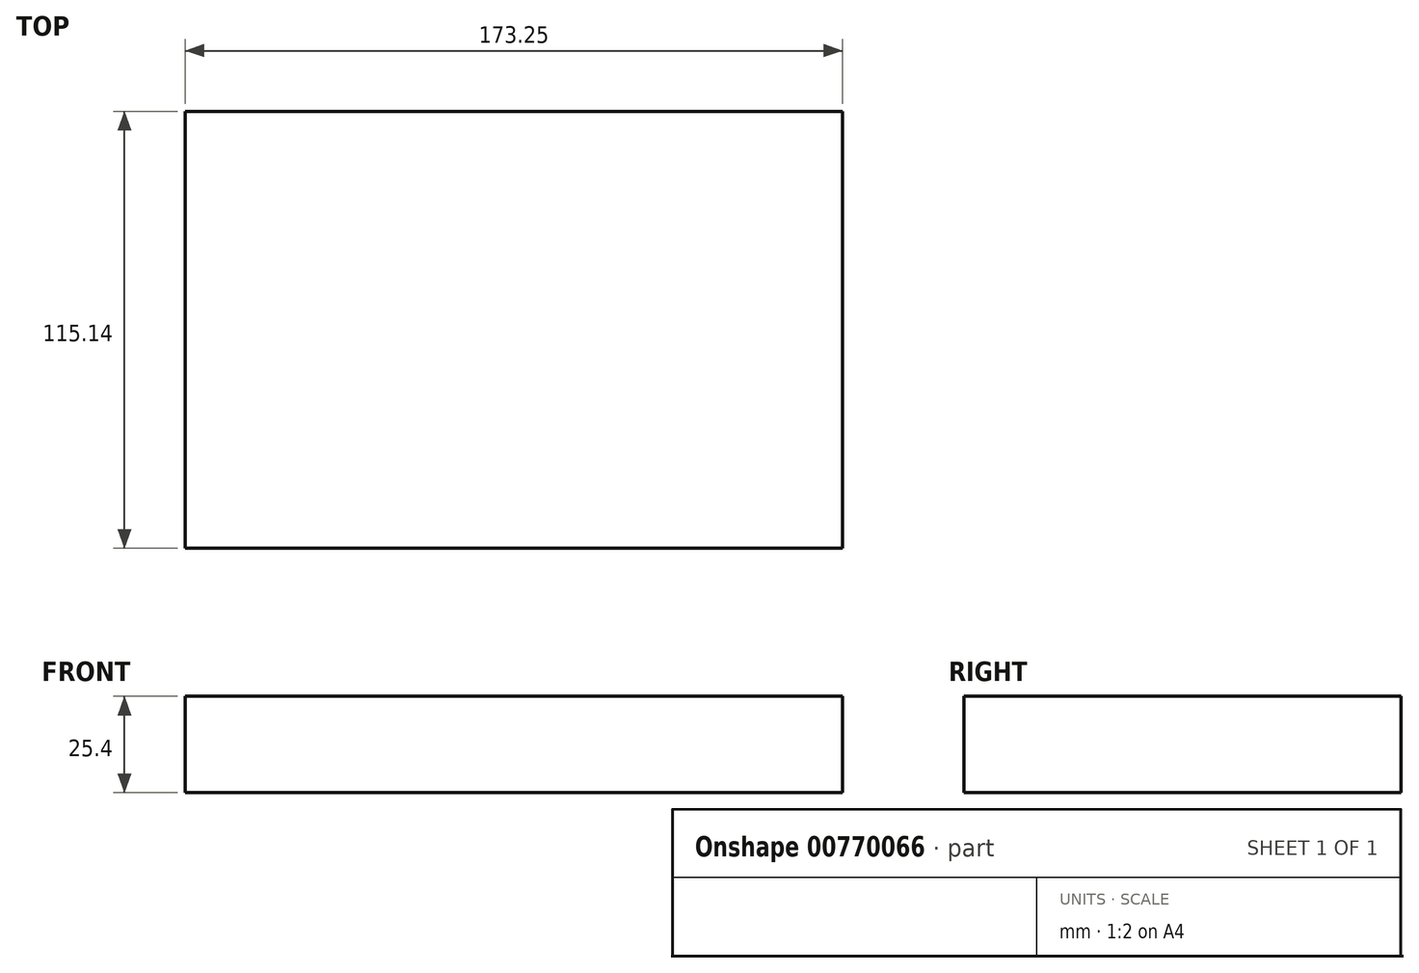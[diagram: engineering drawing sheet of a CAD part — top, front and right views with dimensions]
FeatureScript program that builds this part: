
annotation { "Feature Type Name" : "Feature", "Feature Type Description" : "" }
export const myFeature = defineFeature(function(context is Context, id is Id, definition is map)
    precondition{}
    {
        {
            var Q0;
            Q0=qCreatedBy(makeId("Top.planeOp"),FACE);
            var sketch = newSketch(context, id + "F0", { "sketchPlane" : qUnion([Q0])});
            skLineSegment(sketch, "E0.bottom", {"start": v(56.33, 42.52) * mm, "end": v(-116.92, 42.52) * mm});
            skLineSegment(sketch, "E0.top", {"start": v(56.33, -72.62) * mm, "end": v(-116.92, -72.62) * mm});
            skLineSegment(sketch, "E0.left", {"start": v(56.33, 42.52) * mm, "end": v(56.33, -72.62) * mm});
            skLineSegment(sketch, "E0.right", {"start": v(-116.92, 42.52) * mm, "end": v(-116.92, -72.62) * mm});
            skSolve(sketch);
        }
        {
            var Q0;
            Q0=makeQuery(id+"F0.imprint","IMPRINT",FACE,{"disambiguationData":[TD([[makeQuery(id+"F0.imprint","IMPRINT",EDGE,{"derivedFrom":sQuery(id+"F0.wireOp",EDGE,"E0.bottom")}),1.0]])]});
            extrude(context, id + "F1", {"entities" : qUnion([Q0]), "depth" : 25.4 * mm, "offsetDistance" : 25.4 * mm});
        }
    });
